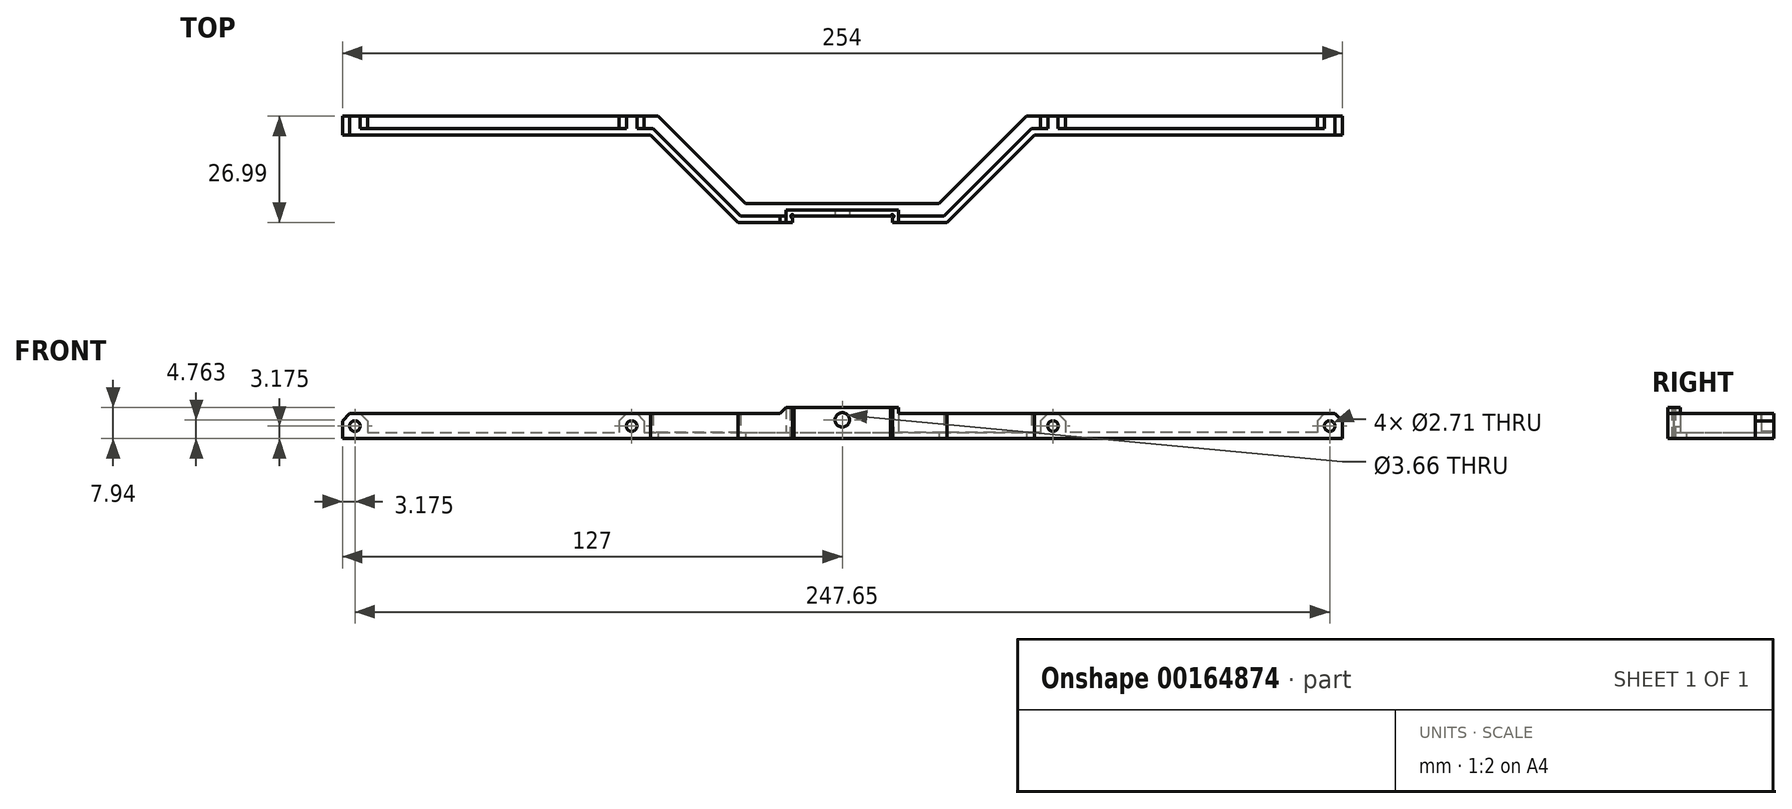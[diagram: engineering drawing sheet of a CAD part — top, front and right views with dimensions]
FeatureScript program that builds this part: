
annotation { "Feature Type Name" : "Feature", "Feature Type Description" : "" }
export const myFeature = defineFeature(function(context is Context, id is Id, definition is map)
    precondition{}
    {
        {
            var Q0;
            Q0=qCreatedBy(makeId("Top.planeOp"),FACE);
            var sketch = newSketch(context, id + "F0", { "sketchPlane" : qUnion([Q0])});
            skLineSegment(sketch, "E0", {"start": v(-127, 22.22) * mm, "end": v(-46.78, 22.22) * mm});
            skLineSegment(sketch, "E1", {"start": v(-46.78, 22.23) * mm, "end": v(-24.56, 0) * mm});
            skLineSegment(sketch, "E2", {"start": v(-24.56, 0) * mm, "end": v(24.56, 0) * mm});
            skLineSegment(sketch, "E3", {"start": v(24.56, 0) * mm, "end": v(46.78, 22.23) * mm});
            skLineSegment(sketch, "E4", {"start": v(46.78, 22.22) * mm, "end": v(127, 22.22) * mm});
            skLineSegment(sketch, "E5", {"start": v(-127, 22.23) * mm, "end": v(-127, 17.46) * mm});
            skLineSegment(sketch, "E6", {"start": v(-127, 17.46) * mm, "end": v(-48.76, 17.46) * mm});
            skLineSegment(sketch, "E7", {"start": v(-48.76, 17.46) * mm, "end": v(-26.53, -4.76) * mm});
            skLineSegment(sketch, "E8", {"start": v(-26.53, -4.76) * mm, "end": v(26.53, -4.76) * mm});
            skLineSegment(sketch, "E9", {"start": v(26.53, -4.76) * mm, "end": v(48.76, 17.46) * mm});
            skLineSegment(sketch, "E10", {"start": v(48.76, 17.46) * mm, "end": v(127, 17.46) * mm});
            skLineSegment(sketch, "E11", {"start": v(127, 17.46) * mm, "end": v(127, 22.23) * mm});
            skLineSegment(sketch, "E12", {"start": v(-35.67, 11.11) * mm, "end": v(-39.04, 7.74) * mm, "construction": true});
            skLineSegment(sketch, "E13", {"start": v(0, 0) * mm, "end": v(0, -4.76) * mm, "construction": true});
            skLineSegment(sketch, "E14", {"start": v(35.67, 11.11) * mm, "end": v(39.04, 7.74) * mm, "construction": true});
            skLineSegment(sketch, "E15", {"start": v(-46.78, 22.22) * mm, "end": v(46.78, 22.22) * mm, "construction": true});
            skLineSegment(sketch, "E16", {"start": v(0, 0) * mm, "end": v(0, 22.22) * mm, "construction": true});
            skSolve(sketch);
        }
        {
            var Q0;
            Q0=qSketchRegion(id+"F0",true);
            extrude(context, id + "F1", {"entities" : qUnion([Q0]), "depth" : 1.59 * mm});
        }
        {
            var Q0;
            Q0=makeQuery(id+"F1.opExtrude","CAP_FACE",FACE,{"disambiguationData":[OSD([sQuery(id+"F0.wireOp",EDGE,"E0"),sQuery(id+"F0.wireOp",EDGE,"E1"),sQuery(id+"F0.wireOp",EDGE,"E2"),sQuery(id+"F0.wireOp",EDGE,"E3"),sQuery(id+"F0.wireOp",EDGE,"E4"),sQuery(id+"F0.wireOp",EDGE,"E5"),sQuery(id+"F0.wireOp",EDGE,"E6"),sQuery(id+"F0.wireOp",EDGE,"E7"),sQuery(id+"F0.wireOp",EDGE,"E8"),sQuery(id+"F0.wireOp",EDGE,"E9"),sQuery(id+"F0.wireOp",EDGE,"E10"),sQuery(id+"F0.wireOp",EDGE,"E11")])],"isStart":false});
            var sketch = newSketch(context, id + "F2", { "sketchPlane" : qUnion([Q0])});
            skLineSegment(sketch, "E17.bottom", {"start": v(-127, 17.46) * mm, "end": v(-48.76, 17.46) * mm});
            skLineSegment(sketch, "E17.top", {"start": v(-127, 19.05) * mm, "end": v(-48.1, 19.05) * mm});
            skLineSegment(sketch, "E17.left", {"start": v(-127, 17.46) * mm, "end": v(-127, 19.05) * mm});
            skLineSegment(sketch, "E18", {"start": v(-48.76, 17.46) * mm, "end": v(-26.53, -4.76) * mm});
            skLineSegment(sketch, "E19", {"start": v(-26.53, -4.76) * mm, "end": v(26.53, -4.76) * mm});
            skLineSegment(sketch, "E20", {"start": v(26.53, -4.76) * mm, "end": v(48.76, 17.46) * mm});
            skLineSegment(sketch, "E21", {"start": v(48.76, 17.46) * mm, "end": v(127, 17.46) * mm});
            skLineSegment(sketch, "E22", {"start": v(127, 17.46) * mm, "end": v(127, 19.05) * mm});
            skLineSegment(sketch, "E23", {"start": v(127, 19.05) * mm, "end": v(48.1, 19.05) * mm});
            skLineSegment(sketch, "E24", {"start": v(48.1, 19.05) * mm, "end": v(25.87, -3.17) * mm});
            skLineSegment(sketch, "E25", {"start": v(-25.87, -3.18) * mm, "end": v(-48.1, 19.05) * mm});
            skLineSegment(sketch, "E26", {"start": v(-37.64, 6.35) * mm, "end": v(-36.52, 7.47) * mm, "construction": true});
            skLineSegment(sketch, "E27", {"start": v(37.64, 6.35) * mm, "end": v(36.52, 7.47) * mm, "construction": true});
            skLineSegment(sketch, "E28", {"start": v(0, -3.18) * mm, "end": v(0, -4.76) * mm, "construction": true});
            skLineSegment(sketch, "E29", {"start": v(-25.87, -3.18) * mm, "end": v(-14.29, -3.18) * mm});
            skLineSegment(sketch, "E30", {"start": v(25.87, -3.17) * mm, "end": v(14.29, -3.17) * mm});
            skLineSegment(sketch, "E31.bottom", {"start": v(-14.29, -3.18) * mm, "end": v(14.29, -3.18) * mm, "construction": true});
            skLineSegment(sketch, "E31.top", {"start": v(-14.29, -1.59) * mm, "end": v(14.29, -1.59) * mm});
            skLineSegment(sketch, "E31.left", {"start": v(-14.29, -3.18) * mm, "end": v(-14.29, -1.59) * mm});
            skLineSegment(sketch, "E31.right", {"start": v(14.29, -3.18) * mm, "end": v(14.29, -1.59) * mm});
            skSolve(sketch);
        }
        {
            var Q0;
            Q0=qSketchRegion(id+"F2",true);
            extrude(context, id + "F3", {"entities" : qUnion([Q0]), "operationType" : NewBodyOperationType.ADD, "depth" : 4.76 * mm});
        }
        {
            var Q0;
            Q0=makeQuery(id+"F3.opExtrude","SWEPT_FACE",FACE,{"disambiguationData":[OSD([sQuery(id+"F2.wireOp",EDGE,"E17.top")])]});
            var sketch = newSketch(context, id + "F4", { "sketchPlane" : qUnion([Q0])});
            skLineSegment(sketch, "E32.bottom", {"start": v(-50.34, 6.35) * mm, "end": v(-56.7, 6.35) * mm});
            skLineSegment(sketch, "E32.top", {"start": v(-50.34, 0) * mm, "end": v(-56.7, 0) * mm});
            skLineSegment(sketch, "E32.left", {"start": v(-50.34, 6.35) * mm, "end": v(-50.34, 0) * mm});
            skLineSegment(sketch, "E32.right", {"start": v(-56.7, 6.35) * mm, "end": v(-56.7, 0) * mm});
            skLineSegment(sketch, "E33", {"start": v(-50.34, 3.18) * mm, "end": v(-48.76, 3.18) * mm, "construction": true});
            skLineSegment(sketch, "E34.bottom", {"start": v(-127, 6.35) * mm, "end": v(-120.65, 6.35) * mm});
            skLineSegment(sketch, "E34.top", {"start": v(-127, 0) * mm, "end": v(-120.65, 0) * mm});
            skLineSegment(sketch, "E34.left", {"start": v(-127, 6.35) * mm, "end": v(-127, 0) * mm});
            skLineSegment(sketch, "E34.right", {"start": v(-120.65, 6.35) * mm, "end": v(-120.65, 0) * mm});
            skLineSegment(sketch, "E35.bottom", {"start": v(127, 6.35) * mm, "end": v(120.65, 6.35) * mm});
            skLineSegment(sketch, "E35.top", {"start": v(127, 0) * mm, "end": v(120.65, 0) * mm});
            skLineSegment(sketch, "E35.left", {"start": v(127, 6.35) * mm, "end": v(127, 0) * mm});
            skLineSegment(sketch, "E35.right", {"start": v(120.65, 6.35) * mm, "end": v(120.65, 0) * mm});
            skLineSegment(sketch, "E36.bottom", {"start": v(50.34, 6.35) * mm, "end": v(56.7, 6.35) * mm});
            skLineSegment(sketch, "E36.top", {"start": v(50.34, 0) * mm, "end": v(56.7, 0) * mm});
            skLineSegment(sketch, "E36.left", {"start": v(50.34, 6.35) * mm, "end": v(50.34, 0) * mm});
            skLineSegment(sketch, "E36.right", {"start": v(56.7, 6.35) * mm, "end": v(56.7, 0) * mm});
            skLineSegment(sketch, "E37", {"start": v(120.65, 3.18) * mm, "end": v(56.7, 3.18) * mm, "construction": true});
            skLineSegment(sketch, "E38", {"start": v(-56.7, 3.18) * mm, "end": v(-120.65, 3.17) * mm, "construction": true});
            skSolve(sketch);
        }
        {
            var Q0;
            Q0=qSketchRegion(id+"F4",true);
            var Q1;
            Q1=makeQuery(id+"F1.opExtrude","SWEPT_FACE",FACE,{"disambiguationData":[OSD([sQuery(id+"F0.wireOp",EDGE,"E0")])]});
            extrude(context, id + "F5", {"entities" : qUnion([Q0]), "operationType" : NewBodyOperationType.ADD, "endBound" : BoundingType.UP_TO_SURFACE, "endBoundEntityFace" : qUnion([Q1]), "depth" : 25.4 * mm});
        }
        {
            var Q0;
            Q0=makeQuery(id+"F5.boolean.opBoolean","MERGE",EDGE,{"derivedFrom":[makeQuery(id+"F3.opExtrude","CAP_EDGE",EDGE,{"disambiguationData":[OSD([sQuery(id+"F2.wireOp",EDGE,"E17.left")])],"isStart":false}),makeQuery(id+"F5.opExtrude","SWEPT_EDGE",EDGE,{"disambiguationData":[OSD([sQuery(id+"F4.wireOp",EDGE,"E35.bottom"),sQuery(id+"F4.wireOp",EDGE,"E35.left")])]})]});
            var Q1;
            Q1=makeQuery(id+"F5.opExtrude","SWEPT_EDGE",EDGE,{"disambiguationData":[OSD([sQuery(id+"F2.wireOp",EDGE,"E17.top"),sQuery(id+"F4.wireOp",EDGE,"E35.bottom"),sQuery(id+"F4.wireOp",EDGE,"E35.right")])]});
            var Q2;
            Q2=makeQuery(id+"F5.opExtrude","SWEPT_EDGE",EDGE,{"disambiguationData":[OSD([sQuery(id+"F2.wireOp",EDGE,"E17.top"),sQuery(id+"F4.wireOp",EDGE,"E36.bottom"),sQuery(id+"F4.wireOp",EDGE,"E36.right")])]});
            var Q3;
            Q3=makeQuery(id+"F5.opExtrude","SWEPT_EDGE",EDGE,{"disambiguationData":[OSD([sQuery(id+"F2.wireOp",EDGE,"E17.top"),sQuery(id+"F4.wireOp",EDGE,"E36.bottom"),sQuery(id+"F4.wireOp",EDGE,"E36.left")])]});
            var Q4;
            Q4=makeQuery(id+"F5.opExtrude","SWEPT_EDGE",EDGE,{"disambiguationData":[OSD([sQuery(id+"F4.wireOp",EDGE,"E32.bottom"),sQuery(id+"F4.wireOp",EDGE,"E32.left")])]});
            var Q5;
            Q5=makeQuery(id+"F5.opExtrude","SWEPT_EDGE",EDGE,{"disambiguationData":[OSD([sQuery(id+"F4.wireOp",EDGE,"E32.bottom"),sQuery(id+"F4.wireOp",EDGE,"E32.right")])]});
            var Q6;
            Q6=makeQuery(id+"F5.opExtrude","SWEPT_EDGE",EDGE,{"disambiguationData":[OSD([sQuery(id+"F4.wireOp",EDGE,"E34.bottom"),sQuery(id+"F4.wireOp",EDGE,"E34.right")])]});
            var Q7;
            Q7=makeQuery(id+"F5.boolean.opBoolean","MERGE",EDGE,{"derivedFrom":[makeQuery(id+"F3.opExtrude","CAP_EDGE",EDGE,{"disambiguationData":[OSD([sQuery(id+"F2.wireOp",EDGE,"E22")])],"isStart":false}),makeQuery(id+"F5.opExtrude","SWEPT_EDGE",EDGE,{"disambiguationData":[OSD([sQuery(id+"F4.wireOp",EDGE,"E34.bottom"),sQuery(id+"F4.wireOp",EDGE,"E34.left")])]})]});
            chamfer(context, id + "F6", {"entities" : qUnion([Q0, Q1, Q2, Q3, Q4, Q5, Q6, Q7]), "width" : 1.86 * mm, "tangentPropagation" : true});
        }
        {
            var Q0;
            Q0=makeQuery(id+"F5.boolean.opBoolean","MERGE",FACE,{"derivedFrom":[makeQuery(id+"F3.opExtrude","CAP_FACE",FACE,{"disambiguationData":[OSD([sQuery(id+"F2.wireOp",EDGE,"E17.bottom"),sQuery(id+"F2.wireOp",EDGE,"E17.top"),sQuery(id+"F2.wireOp",EDGE,"E17.left"),sQuery(id+"F2.wireOp",EDGE,"E18"),sQuery(id+"F2.wireOp",EDGE,"E19"),sQuery(id+"F2.wireOp",EDGE,"E20"),sQuery(id+"F2.wireOp",EDGE,"E21"),sQuery(id+"F2.wireOp",EDGE,"E22"),sQuery(id+"F2.wireOp",EDGE,"E23"),sQuery(id+"F2.wireOp",EDGE,"E24"),sQuery(id+"F2.wireOp",EDGE,"E25"),sQuery(id+"F2.wireOp",EDGE,"E29"),sQuery(id+"F2.wireOp",EDGE,"E30"),sQuery(id+"F2.wireOp",EDGE,"E31.top"),sQuery(id+"F2.wireOp",EDGE,"E31.left"),sQuery(id+"F2.wireOp",EDGE,"E31.right")])],"isStart":false}),makeQuery(id+"F5.opExtrude","SWEPT_FACE",FACE,{"disambiguationData":[OSD([sQuery(id+"F4.wireOp",EDGE,"E32.bottom")])]}),makeQuery(id+"F5.opExtrude","SWEPT_FACE",FACE,{"disambiguationData":[OSD([sQuery(id+"F4.wireOp",EDGE,"E34.bottom")])]}),makeQuery(id+"F5.opExtrude","SWEPT_FACE",FACE,{"disambiguationData":[OSD([sQuery(id+"F4.wireOp",EDGE,"E35.bottom")])]}),makeQuery(id+"F5.opExtrude","SWEPT_FACE",FACE,{"disambiguationData":[OSD([sQuery(id+"F4.wireOp",EDGE,"E36.bottom")])]})]});
            var sketch = newSketch(context, id + "F7", { "sketchPlane" : qUnion([Q0])});
            skLineSegment(sketch, "E39.bottom", {"start": v(-14.29, -1.59) * mm, "end": v(14.29, -1.59) * mm});
            skLineSegment(sketch, "E39.top", {"start": v(-14.29, -4.76) * mm, "end": v(14.29, -4.76) * mm});
            skLineSegment(sketch, "E39.left", {"start": v(-14.29, -1.59) * mm, "end": v(-14.29, -4.76) * mm});
            skLineSegment(sketch, "E39.right", {"start": v(14.29, -1.59) * mm, "end": v(14.29, -4.76) * mm});
            skSolve(sketch);
        }
        {
            var Q0;
            Q0=qSketchRegion(id+"F7",true);
            extrude(context, id + "F8", {"entities" : qUnion([Q0]), "operationType" : NewBodyOperationType.ADD, "depth" : 1.59 * mm});
        }
        {
            var Q0;
            Q0=makeQuery(id+"F8.opExtrude","CAP_FACE",FACE,{"disambiguationData":[OSD([sQuery(id+"F7.wireOp",EDGE,"E39.bottom"),sQuery(id+"F7.wireOp",EDGE,"E39.top"),sQuery(id+"F7.wireOp",EDGE,"E39.left"),sQuery(id+"F7.wireOp",EDGE,"E39.right")])],"isStart":false});
            var sketch = newSketch(context, id + "F9", { "sketchPlane" : qUnion([Q0])});
            skLineSegment(sketch, "E40.bottom", {"start": v(-12.7, -4.76) * mm, "end": v(12.7, -4.76) * mm});
            skLineSegment(sketch, "E40.top", {"start": v(-12.7, -3.18) * mm, "end": v(12.7, -3.18) * mm});
            skLineSegment(sketch, "E40.left", {"start": v(-12.7, -4.76) * mm, "end": v(-12.7, -3.18) * mm});
            skLineSegment(sketch, "E40.right", {"start": v(12.7, -4.76) * mm, "end": v(12.7, -3.18) * mm});
            skLineSegment(sketch, "E41.bottom", {"start": v(-12.7, -3.18) * mm, "end": v(-14.29, -3.18) * mm, "construction": true});
            skLineSegment(sketch, "E41.top", {"start": v(-12.7, -1.59) * mm, "end": v(-14.29, -1.59) * mm, "construction": true});
            skLineSegment(sketch, "E41.left", {"start": v(-12.7, -3.18) * mm, "end": v(-12.7, -1.59) * mm, "construction": true});
            skLineSegment(sketch, "E41.right", {"start": v(-14.29, -3.18) * mm, "end": v(-14.29, -1.59) * mm, "construction": true});
            skLineSegment(sketch, "E42.bottom", {"start": v(12.7, -3.18) * mm, "end": v(14.29, -3.18) * mm, "construction": true});
            skLineSegment(sketch, "E42.top", {"start": v(12.7, -1.59) * mm, "end": v(14.29, -1.59) * mm, "construction": true});
            skLineSegment(sketch, "E42.left", {"start": v(12.7, -3.18) * mm, "end": v(12.7, -1.59) * mm, "construction": true});
            skLineSegment(sketch, "E42.right", {"start": v(14.29, -3.18) * mm, "end": v(14.29, -1.59) * mm, "construction": true});
            skSolve(sketch);
        }
        {
            var Q0;
            Q0=qSketchRegion(id+"F9",true);
            var Q1;
            Q1=makeQuery(id+"F1.opExtrude","CAP_FACE",FACE,{"disambiguationData":[OSD([sQuery(id+"F0.wireOp",EDGE,"E0"),sQuery(id+"F0.wireOp",EDGE,"E1"),sQuery(id+"F0.wireOp",EDGE,"E2"),sQuery(id+"F0.wireOp",EDGE,"E3"),sQuery(id+"F0.wireOp",EDGE,"E4"),sQuery(id+"F0.wireOp",EDGE,"E5"),sQuery(id+"F0.wireOp",EDGE,"E6"),sQuery(id+"F0.wireOp",EDGE,"E7"),sQuery(id+"F0.wireOp",EDGE,"E8"),sQuery(id+"F0.wireOp",EDGE,"E9"),sQuery(id+"F0.wireOp",EDGE,"E10"),sQuery(id+"F0.wireOp",EDGE,"E11")])],"isStart":true});
            extrude(context, id + "F10", {"entities" : qUnion([Q0]), "operationType" : NewBodyOperationType.REMOVE, "endBound" : BoundingType.UP_TO_SURFACE, "oppositeDirection" : true, "endBoundEntityFace" : qUnion([Q1]), "depth" : 25.4 * mm});
        }
        {
            var Q0;
            Q0=makeQuery(id+"F10.boolean.opBoolean","COPY",FACE,{"derivedFrom":makeQuery(id+"F10.opExtrude","SWEPT_FACE",FACE,{"disambiguationData":[OSD([sQuery(id+"F9.wireOp",EDGE,"E40.top")])]})});
            var sketch = newSketch(context, id + "F11", { "sketchPlane" : qUnion([Q0])});
            skLineSegment(sketch, "E43", {"start": v(123.82, 6.35) * mm, "end": v(123.82, 0) * mm, "construction": true});
            skLineSegment(sketch, "E44", {"start": v(53.52, 6.35) * mm, "end": v(53.52, 0) * mm, "construction": true});
            skCircle(sketch, "E45", {"center": v(53.52, 3.18) * mm, "radius": 1.35 * mm});
            skCircle(sketch, "E46", {"center": v(123.82, 3.18) * mm, "radius": 1.35 * mm});
            skLineSegment(sketch, "E47", {"start": v(-53.52, 6.35) * mm, "end": v(-53.52, 0) * mm, "construction": true});
            skLineSegment(sketch, "E48", {"start": v(-123.83, 6.35) * mm, "end": v(-123.83, 0) * mm, "construction": true});
            skCircle(sketch, "E49", {"center": v(-123.83, 3.18) * mm, "radius": 1.35 * mm});
            skCircle(sketch, "E50", {"center": v(-53.52, 3.18) * mm, "radius": 1.35 * mm});
            skLineSegment(sketch, "E51", {"start": v(0, 7.94) * mm, "end": v(0, 4.76) * mm, "construction": true});
            skCircle(sketch, "E52", {"center": v(0, 4.76) * mm, "radius": 1.83 * mm});
            skSolve(sketch);
        }
        {
            var Q0;
            Q0=qSketchRegion(id+"F11",true);
            var Q1;
            {var subQ0=sQuery(id+"F0.wireOp",EDGE,"E0");Q1=makeQuery(id+"F5.boolean.opBoolean","MERGE",FACE,{"derivedFrom":[makeQuery(id+"F1.opExtrude","SWEPT_FACE",FACE,{"disambiguationData":[OSD([subQ0])]}),makeQuery(id+"F5.opExtrude","CAP_FACE",FACE,{"disambiguationData":[OSD([subQ0]),ownerDisambiguation([makeQuery(id+"F5.opExtrude","SWEPT_BODY",BODY,{"disambiguationData":[OSD([sQuery(id+"F4.wireOp",EDGE,"E35.bottom"),sQuery(id+"F4.wireOp",EDGE,"E35.top"),sQuery(id+"F4.wireOp",EDGE,"E35.left"),sQuery(id+"F4.wireOp",EDGE,"E35.right")])]})])],"isStart":false}),makeQuery(id+"F5.opExtrude","CAP_FACE",FACE,{"disambiguationData":[OSD([subQ0]),ownerDisambiguation([makeQuery(id+"F5.opExtrude","SWEPT_BODY",BODY,{"disambiguationData":[OSD([sQuery(id+"F4.wireOp",EDGE,"E36.bottom"),sQuery(id+"F4.wireOp",EDGE,"E36.top"),sQuery(id+"F4.wireOp",EDGE,"E36.left"),sQuery(id+"F4.wireOp",EDGE,"E36.right")])]})])],"isStart":false})]});}
            extrude(context, id + "F12", {"entities" : qUnion([Q0]), "operationType" : NewBodyOperationType.REMOVE, "endBound" : BoundingType.UP_TO_SURFACE, "oppositeDirection" : true, "endBoundEntityFace" : qUnion([Q1]), "depth" : 25.4 * mm});
        }
        {
            var Q0;
            Q0=makeQuery(id+"F8.opExtrude","CAP_EDGE",EDGE,{"disambiguationData":[OSD([sQuery(id+"F7.wireOp",EDGE,"E39.left")])],"isStart":true});
            var Q1;
            Q1=makeQuery(id+"F8.opExtrude","CAP_EDGE",EDGE,{"disambiguationData":[OSD([sQuery(id+"F7.wireOp",EDGE,"E39.right")])],"isStart":true});
            chamfer(context, id + "F13", {"entities" : qUnion([Q0, Q1]), "width" : 1.59 * mm, "tangentPropagation" : true});
        }
        {
            var Q0;
            Q0=makeQuery(id+"F8.opExtrude","CAP_FACE",FACE,{"disambiguationData":[OSD([sQuery(id+"F7.wireOp",EDGE,"E39.bottom"),sQuery(id+"F7.wireOp",EDGE,"E39.top"),sQuery(id+"F7.wireOp",EDGE,"E39.left"),sQuery(id+"F7.wireOp",EDGE,"E39.right")])],"isStart":false});
            var sketch = newSketch(context, id + "F14", { "sketchPlane" : qUnion([Q0])});
            skCircle(sketch, "E53", {"center": v(-12.7, -3.18) * mm, "radius": 0.4 * mm});
            skCircle(sketch, "E54", {"center": v(12.7, -3.18) * mm, "radius": 0.4 * mm});
            skSolve(sketch);
        }
        {
            var Q0;
            Q0 = qSketchRegion(id + "F14", true);
            var Q1;
            Q1=makeQuery(id+"F1.opExtrude","CAP_FACE",FACE,{"disambiguationData":[OSD([sQuery(id+"F0.wireOp",EDGE,"E0"),sQuery(id+"F0.wireOp",EDGE,"E1"),sQuery(id+"F0.wireOp",EDGE,"E2"),sQuery(id+"F0.wireOp",EDGE,"E3"),sQuery(id+"F0.wireOp",EDGE,"E4"),sQuery(id+"F0.wireOp",EDGE,"E5"),sQuery(id+"F0.wireOp",EDGE,"E6"),sQuery(id+"F0.wireOp",EDGE,"E7"),sQuery(id+"F0.wireOp",EDGE,"E8"),sQuery(id+"F0.wireOp",EDGE,"E9"),sQuery(id+"F0.wireOp",EDGE,"E10"),sQuery(id+"F0.wireOp",EDGE,"E11")])],"isStart":true});
            extrude(context, id + "F15", {"entities" : qUnion([Q0]), "operationType" : NewBodyOperationType.REMOVE, "endBound" : BoundingType.UP_TO_SURFACE, "oppositeDirection" : true, "endBoundEntityFace" : qUnion([Q1]), "depth" : 25.4 * mm});
        }
    });
